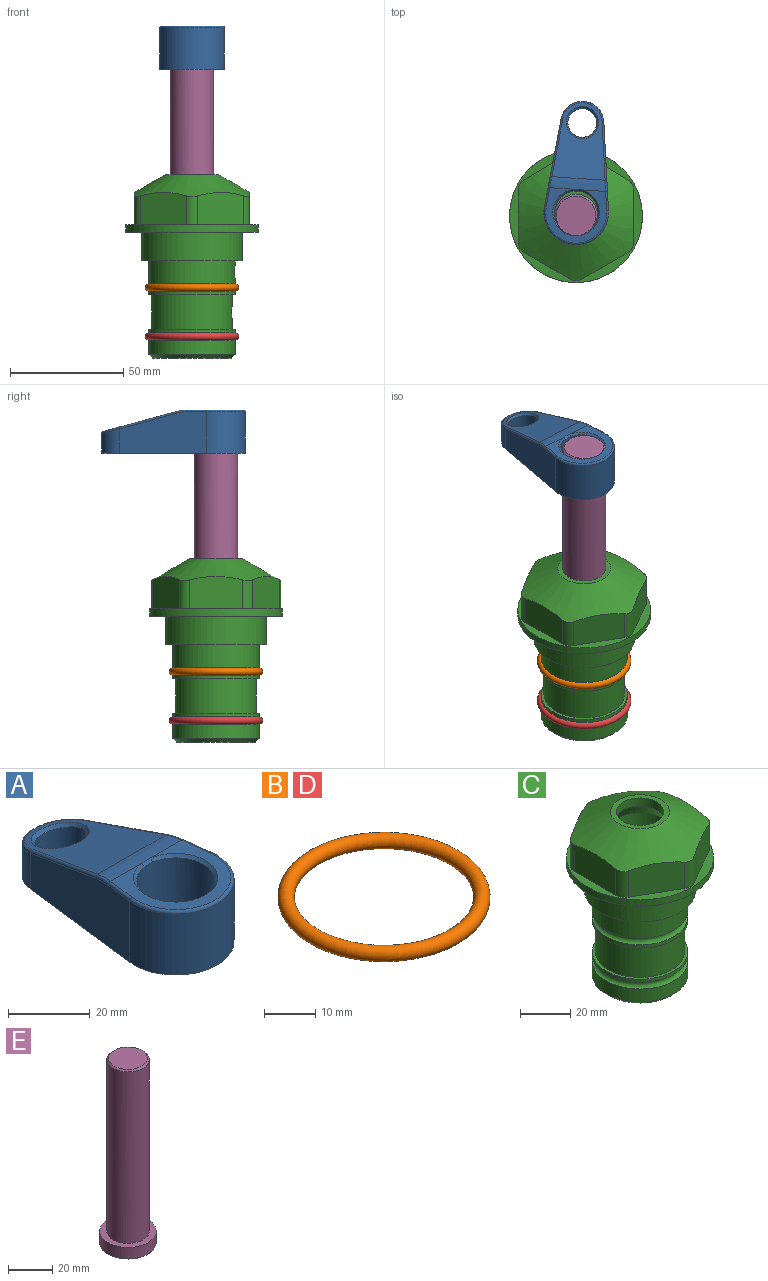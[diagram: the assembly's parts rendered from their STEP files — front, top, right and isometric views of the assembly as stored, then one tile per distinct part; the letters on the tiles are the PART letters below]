
ASSEMBLY  parts=5 mates=4
PART A: 31 faces, bbox 31.7x65.5x19.8 mm
  f0: plane 39.12x18.26mm, normal (0.99,0.12,0), area 612.2mm2, adj f1,f4,f7,f11,f13,f15
  f1: cylinder r=9.53mm len=18.91mm, axis (0,0,-1), area 296.1mm2, adj f0,f2,f7,f17
  f2: plane 39.12x18.26mm, normal (-0.99,0.12,0), area 612.2mm2, adj f1,f4,f7,f12,f14,f16
  f3: cylinder r=6.35mm len=12.7mm, axis (0,0,-1), area 362.4mm2, adj f7,f18
  f4: cylinder r=14.29mm len=28.58mm, axis (0,0,-1), area 882.2mm2, adj f0,f2,f7,f10
  f5: cylinder r=9.53mm len=19.05mm, axis (0,0,-1), area 1092.6mm2, adj f7,f19,f20
  f6: plane 26.99x23.69mm, normal (0,0,1), area 216.2mm2, adj f9,f10,f11,f12,f19
  f7: plane 63.5x28.58mm, normal (0,0,-1), area 661.8mm2, adj f0,f1,f2,f3,f4,f5,f22,f23
  f8: plane 33.52x23.6mm, normal (0,0.26,0.97), area 486mm2, adj f9,f15,f16,f17,f18
  f9: cylinder r=19.05mm len=24.72mm, axis (1,0,0), area 120.4mm2, adj f6,f8,f13,f14,f20
  f10: torus R=13.49mm, axis (0,0,1), area 59mm2, adj f4,f6,f11,f12
  f11: cylinder r=0.79mm len=8.67mm, axis (0.12,-0.99,0), area 10.8mm2, adj f0,f6,f10,f13
  f12: cylinder r=0.79mm len=8.67mm, axis (0.12,0.99,0), area 10.8mm2, adj f2,f6,f10,f14
  f13: bspline ~4.95x1.42mm, area 6.1mm2, adj f0,f9,f11,f15
  f14: bspline ~4.95x1.42mm, area 6.1mm2, adj f2,f9,f12,f16
  f15: cylinder r=0.79mm len=25.95mm, axis (0.12,-0.96,0.26), area 32.9mm2, adj f0,f8,f13,f17
  f16: cylinder r=0.79mm len=25.95mm, axis (0.12,0.96,-0.26), area 32.9mm2, adj f2,f8,f14,f17
  f17: bspline ~18.91x8.38mm, area 30mm2, adj f1,f8,f15,f16
  f18: bspline ~14.29x14.29mm, area 48.3mm2, adj f3,f8
  f19: cone r=9.53mm half-angle=45deg, axis (0,0,1), area 66.5mm2, adj f5,f6,f20
  f20: bspline ~3.22x0.96mm, area 3.5mm2, adj f5,f9,f19
  f21: plane 2.75x2.72mm, normal (0,0,-1), area 2.9mm2, adj f23,f25,f28
  f22: plane 23.05x15.88mm, normal (-0.99,-0.12,0), area 323.6mm2, adj f7,f25,f26,f27,f28,f29
  f23: plane 23.05x15.88mm, normal (0.99,-0.12,0), area 323.6mm2, adj f7,f21,f25,f27,f28,f30
  f24: cylinder r=9.53mm len=10.69mm, axis (0,0,-1), area 114.7mm2, adj f7,f27,f29,f30
  f25: cylinder r=12.7mm len=20.59mm, axis (0,0,-1), area 381.1mm2, adj f7,f21,f22,f23,f26,f28
  f26: plane 2.75x2.72mm, normal (0,0,-1), area 2.9mm2, adj f22,f25,f28
  f27: plane 19.72x18.37mm, normal (0,-0.26,-0.97), area 291.8mm2, adj f22,f23,f24,f28,f29,f30
  f28: cylinder r=15.88mm len=19.92mm, axis (1,0,0), area 54.8mm2, adj f21,f22,f23,f25,f26,f27
  f29: cylinder r=1.59mm len=11mm, axis (0,0,-1), area 34.7mm2, adj f7,f22,f24,f27
  f30: cylinder r=1.59mm len=11mm, axis (0,0,-1), area 34.7mm2, adj f7,f23,f24,f27
PART B: 1 faces, bbox 44.7x44.7x3.2 mm
  f0: torus R=19.05mm, axis (0,0,1), area 1193.9mm2
PART C: 36 faces, bbox 58.7x58.7x81 mm
  f0: cylinder r=17.78mm len=35.56mm, axis (0,0,1), area 1670.8mm2, adj f23,f24,f31
  f1: cylinder r=19.05mm len=38.1mm, axis (0,0,1), area 1191.9mm2, adj f26,f27,f30
  f2: plane 58.66x58.66mm, normal (0,0,-1), area 1150.6mm2, adj f3,f28
  f3: cylinder r=29.33mm len=58.66mm, axis (0,0,-1), area 585.1mm2, adj f2,f4
  f4: plane 58.66x58.66mm, normal (0,0,1), area 475.9mm2, adj f3,f5,f6,f7,f8,f9,f10,f11
  f5: plane 20.32x14.34mm, normal (-0.5,0.87,0), area 324.4mm2, adj f4,f15,f16,f17
  f6: plane 20.32x14.34mm, normal (0.5,0.87,0), area 324.4mm2, adj f4,f14,f15,f17
  f7: plane 23.48x14.34mm, normal (1,0,0), area 324.4mm2, adj f4,f13,f14,f17
  f8: plane 20.32x14.34mm, normal (0.5,-0.87,0), area 324.4mm2, adj f4,f12,f13,f17
  f9: plane 20.32x14.34mm, normal (-0.5,-0.87,0), area 324.4mm2, adj f4,f11,f12,f17
  f10: plane 23.48x14.34mm, normal (-1,0,0), area 324.4mm2, adj f4,f11,f16,f17
  f11: cylinder r=5.08mm len=12.85mm, axis (0,0,-1), area 67.2mm2, adj f4,f9,f10,f17
  f12: cylinder r=5.08mm len=12.85mm, axis (0,0,-1), area 67.2mm2, adj f4,f8,f9,f17
  f13: cylinder r=5.08mm len=12.85mm, axis (0,0,-1), area 67.2mm2, adj f4,f7,f8,f17
  f14: cylinder r=5.08mm len=12.85mm, axis (0,0,-1), area 67.2mm2, adj f4,f6,f7,f17
  f15: cylinder r=5.08mm len=12.85mm, axis (0,0,-1), area 67.2mm2, adj f4,f5,f6,f17
  f16: cylinder r=5.08mm len=12.85mm, axis (0,0,-1), area 67.2mm2, adj f4,f5,f10,f17
  f17: cone r=11.73mm half-angle=60deg, axis (0,0,-1), area 2071.8mm2, adj f5,f6,f7,f8,f9,f10,f11,f12
  f18: plane 23.46x23.46mm, normal (0,0,1), area 147.4mm2, adj f17,f35
  f19: plane 34.93x34.93mm, normal (0,0,-1), area 958mm2, adj f29
  f20: cylinder r=19.05mm len=38.1mm, axis (0,0,1), area 760.1mm2, adj f21,f29
  f21: torus R=19.05mm, axis (0,0,1), area 565.3mm2, adj f20,f22
  f22: cylinder r=19.05mm len=38.1mm, axis (0,0,1), area 190mm2, adj f21,f23
  f23: plane 38.1x38.1mm, normal (0,0,1), area 146.9mm2, adj f0,f22
  f24: plane 38.1x38.1mm, normal (0,0,-1), area 146.9mm2, adj f0,f25
  f25: cylinder r=19.05mm len=38.1mm, axis (0,0,1), area 190mm2, adj f24,f26
  f26: torus R=19.05mm, axis (0,0,1), area 565.3mm2, adj f1,f25
  f27: plane 44.45x44.45mm, normal (0,0,-1), area 411.7mm2, adj f1,f28
  f28: cylinder r=22.23mm len=44.45mm, axis (0,0,1), area 1773.5mm2, adj f2,f27
  f29: cone r=19.05mm half-angle=45deg, axis (0,0,1), area 257.5mm2, adj f19,f20
  f30: cylinder r=3.17mm len=6.75mm, axis (-1,0,0), area 128mm2, adj f1,f33
  f31: cylinder r=3.17mm len=6.35mm, axis (-1,0,0), area 102.5mm2, adj f0,f33
  f32: plane 25.4x25.4mm, normal (0,0,1), area 506.7mm2, adj f33
  f33: cylinder r=12.7mm len=66.42mm, axis (0,0,-1), area 5236.2mm2, adj f30,f31,f32,f34
  f34: cone r=9.53mm half-angle=30deg, axis (0,0,-1), area 443.4mm2, adj f33,f35
  f35: cylinder r=9.53mm len=19.05mm, axis (0,0,-1), area 240.9mm2, adj f18,f34
PART D: same geometry as B
PART E: 6 faces, bbox 25.4x25.4x101.6 mm
  f0: plane 17.46x17.46mm, normal (0,0,1), area 239.5mm2, adj f5
  f1: plane 25.4x25.4mm, normal (0,0,-1), area 506.7mm2, adj f2
  f2: cylinder r=12.7mm len=25.4mm, axis (0,0,1), area 506.7mm2, adj f1,f3
  f3: plane 25.4x25.4mm, normal (0,0,1), area 221.7mm2, adj f2,f4
  f4: cylinder r=9.53mm len=94.46mm, axis (0,0,1), area 5653mm2, adj f3,f5
  f5: cone r=8.73mm half-angle=45deg, axis (0,0,-1), area 64.4mm2, adj f0,f4
PLACE A rot(axis=(0,0,-1),3.9deg) t=(0.1,1.42,27.55)mm
PLACE B at identity
PLACE C at identity fixed
PLACE D t=(0,0,-21.59)mm
PLACE E rot(axis=(0,0,-1),3.9deg) t=(0,0,27.55)mm
MATE fastened D.f0 <-> C.f0  axis (0,0,1) through (0,0,-46.1)mm
MATE fastened A.f6 <-> E.f2  axis (0,0,-1) through (0,0,91.05)mm
MATE fastened B.f0 <-> C.f0  axis (0,0,1) through (0,0,-24.51)mm
MATE cylindrical E.f2 <-> C.f0  axis (0,0,-1) through (0,0,-10.55)mm
